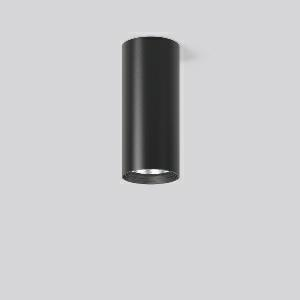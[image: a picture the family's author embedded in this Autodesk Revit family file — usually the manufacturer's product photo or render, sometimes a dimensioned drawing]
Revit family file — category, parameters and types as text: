
# Revit family: heledon_mini_a_931209_003_1_07f0
name_source: partatom
category: Lighting Fixtures
units: mm (PartAtom-declared; Revit-internal decimal feet)

## family parameters
Cut with Voids When Loaded = No
Host = Face
Light Source = No
Part Type = Normal
Room Calculation Point = No
Round Connector Dimension = Use Diameter
Shared = No

## types (1)
- HELEDON mini A (1 x LED Modul 940, 3700 lm, 4000)
    Apparent Load = 29 VA
    Approval mark = CE
    CIE Flux Codes = 99 100 100 100 100
    Color Rendering = 92
    Color Temperature = 4000
    Default Elevation = 1800 mm
    Description = Series: HELEDON mini
Cylindrical surface-mounted downlight. Housing: die-cast aluminium, powder-coated. Internal ceiling frame polycarbonate with bayonet mounting. Black plastic ring and recessed LED to prevent glare from the side. Optical assembly with reflector made of MIRO-Silver with 98% total light reflection for outstanding efficiency - can be changed without tools. Best colour rendering index Ra>90. Suitable for Ceiling mounting. Easy installation with a separate ceiling frame with bayonet mounting and plug connection. Driver integrated. Connected via plug-in connector. High quality converter without flickering and stroboscopic effect. The following accessories can be mounted without use of tools: interchangeable lenses, decorative glasses, honeycomb louvre, clear and frosted diffusers, white interchangeable plastic ring. 
Colour: deep black, matt (RAL 9005)
Diameter: 87 mm
Height: 197 mm
Lamp: LED
Socket: without socket
Colour temperature: 4000K
Colour rendering index (CRI): 92
System power: 29 W
Rated luminous flux: 3700 lm
Luminous efficiency: 128 lm/W
Control gear: Regulated power supply
Protection class: I
Type of protection: IP 20
    Height = 197 mm
    Lamp = 1 x LED Modul 940
    Lamp Light Flux = 3700 lm
    Lamp count = 1
    Length = 87 mm
    Lifetime = 50000 h
    Luminous efficacy = 128 lm/W
    Manufacturer = RZB
    ModVariant = No
    Model = 931209.003.1
    Mounting Place = Ceiling
    Mounting Type = Surface mounted
    Number of Poles = 1
    OnlyDefault = Yes
    Power Factor = 1
    Product Name = HELEDON mini A
    Product group = Surface mounted downlights
    ProductGroupID = 302
    Protection Class = Protection class I
    Protection Degree = IP 20
    RLX_Detail_Level = 1
    RLX_Emergency_Light_Flux = 0 lm
    RLX_Emergency_Type = 0
    RLX_Emergency_Type_DB = No
    RlxData = <blob elided: 107241 chars, md5=234a7fb8>
    Socket = socket
    Standby Power = 0 W
    System Light Flux = 3700 lm
    System Power = 29 W
    Type Comments = Product without accessories
    Type Image = 931188.003.jpg
    URL = http://relux.com
    VarID = ---
    Voltage = 230 V
    Voltage Range = 220-240 V
    Weight = 0.00 kg
    Width = 0 mm  [stored 0 ft]

note: [stored X ft] marks values corroborated as IEEE doubles in the binary element streams (Revit-internal decimal feet)

## geometry (parser evidence)
native form markers: Blend x4, Sweep x10
no freeform markers — native parametric forms only
